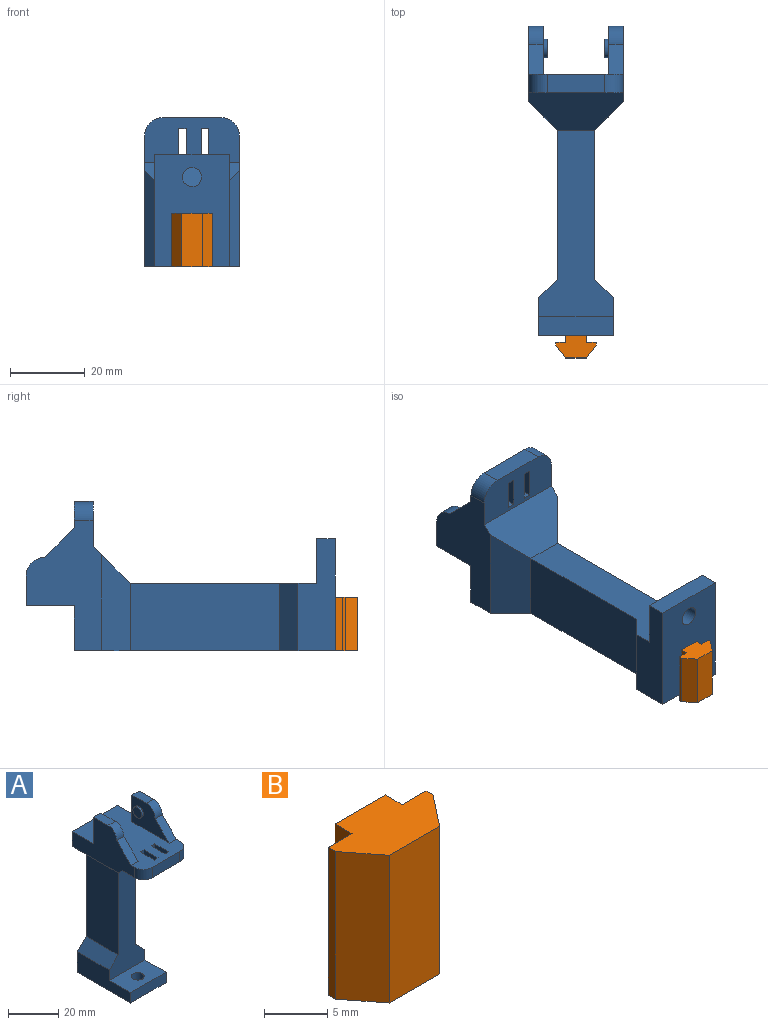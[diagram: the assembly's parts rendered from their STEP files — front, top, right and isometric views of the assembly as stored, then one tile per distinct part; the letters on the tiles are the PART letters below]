
ASSEMBLY  parts=2 mates=1
PART A: 44 faces, bbox 25.5x40x83 mm
  f0: plane 25.5x12mm, normal (0,0,-1), area 263.8mm2, adj f2,f3,f16,f17,f18,f19,f20,f21
  f1: plane 40x25.5mm, normal (0,0,1), area 809.8mm2, adj f2,f3,f5,f6,f8,f9,f16,f17
  f2: plane 15.5x5mm, normal (0,-1,0), area 77.5mm2, adj f0,f1,f25,f27
  f3: plane 35x20.25mm, normal (-1,0,0), area 431.1mm2, adj f0,f1,f5,f7,f14,f24,f25,f39
  f4: plane 8x4mm, normal (0,0,1), area 32mm2, adj f8,f9,f15,f26
  f5: plane 13x4mm, normal (0,1,0), area 52mm2, adj f1,f3,f6,f7
  f6: plane 21x13mm, normal (1,0,0), area 176mm2, adj f1,f5,f7,f12,f14,f41
  f7: plane 8x4mm, normal (0,0,1), area 32mm2, adj f3,f5,f6,f14
  f8: plane 21x13mm, normal (-1,0,0), area 176mm2, adj f1,f4,f9,f10,f15,f40
  f9: plane 13x4mm, normal (0,1,0), area 52mm2, adj f1,f4,f8,f26
  f10: cylinder r=2.5mm len=5mm, axis (1,0,0), area 15.7mm2, adj f8,f11
  f11: plane 5x5mm, normal (-1,0,0), area 19.6mm2, adj f10
  f12: cylinder r=2.5mm len=5mm, axis (-1,0,0), area 15.7mm2, adj f6,f13
  f13: plane 5x5mm, normal (1,0,0), area 19.6mm2, adj f12
  f14: cylinder r=5mm len=5mm, axis (-1,0,0), area 31.4mm2, adj f3,f6,f7,f41
  f15: cylinder r=5mm len=5mm, axis (-1,0,0), area 31.4mm2, adj f4,f8,f26,f40
  f16: plane 7.87x5mm, normal (1,0,0), area 39.4mm2, adj f0,f1,f17,f19
  f17: plane 5x2mm, normal (0,1,0), area 10mm2, adj f0,f1,f16,f18
  f18: plane 7.87x5mm, normal (-1,0,0), area 39.4mm2, adj f0,f1,f17,f19
  f19: plane 5x2mm, normal (0,-1,0), area 10mm2, adj f0,f1,f16,f18
  f20: plane 7.87x5mm, normal (1,0,0), area 39.4mm2, adj f0,f1,f21,f23
  f21: plane 5x2mm, normal (0,1,0), area 10mm2, adj f0,f1,f20,f22
  f22: plane 7.87x5mm, normal (-1,0,0), area 39.4mm2, adj f0,f1,f21,f23
  f23: plane 5x2mm, normal (0,-1,0), area 10mm2, adj f0,f1,f20,f22
  f24: plane 70x25.5mm, normal (0,1,0), area 997.4mm2, adj f1,f3,f26,f28,f30,f32,f33,f34
  f25: cylinder r=5mm len=5mm, axis (0,0,1), area 39.3mm2, adj f0,f1,f2,f3
  f26: plane 35x20.25mm, normal (1,0,0), area 431.1mm2, adj f0,f1,f4,f9,f15,f24,f27,f38
  f27: cylinder r=5mm len=5mm, axis (0,0,1), area 39.3mm2, adj f0,f1,f2,f26
  f28: plane 40x18mm, normal (1,0,0), area 720mm2, adj f24,f29,f36,f38
  f29: plane 50x20mm, normal (0,-1,0), area 575mm2, adj f28,f30,f31,f33,f34,f36,f37,f42
  f30: plane 40x18mm, normal (-1,0,0), area 720mm2, adj f24,f29,f37,f39
  f31: plane 20x12mm, normal (0,0,1), area 219.6mm2, adj f29,f33,f34,f35,f43
  f32: plane 30x20mm, normal (0,0,-1), area 579.6mm2, adj f24,f33,f34,f35,f43
  f33: plane 30x10mm, normal (-1,0,0), area 240mm2, adj f24,f29,f31,f32,f35,f37
  f34: plane 30x10mm, normal (1,0,0), area 240mm2, adj f24,f29,f31,f32,f35,f36
  f35: plane 20x5mm, normal (0,-1,0), area 100mm2, adj f31,f32,f33,f34
  f36: plane 18x5mm, normal (0.71,0,0.71), area 127.3mm2, adj f24,f28,f29,f34
  f37: plane 18x5mm, normal (-0.71,0,0.71), area 127.3mm2, adj f24,f29,f30,f33
  f38: plane 25.75x7.75mm, normal (0.71,0,-0.71), area 239.8mm2, adj f24,f26,f28,f42
  f39: plane 25.75x7.75mm, normal (-0.71,0,-0.71), area 239.8mm2, adj f3,f24,f30,f42
  f40: plane 8x8mm, normal (0,-0.71,0.71), area 45.3mm2, adj f1,f8,f15,f26
  f41: plane 8x8mm, normal (0,-0.71,0.71), area 45.3mm2, adj f1,f3,f6,f14
  f42: plane 25.5x10mm, normal (0,-0.71,-0.71), area 275.7mm2, adj f0,f3,f26,f29,f38,f39
  f43: cylinder r=2.55mm len=5.1mm, axis (0,0,-1), area 80.1mm2, adj f31,f32
PART B: 12 faces, bbox 10.9x6.1x14.3 mm
  f0: plane 14.32x2.65mm, normal (0,1,0), area 38mm2, adj f1,f6,f10,f11
  f1: plane 14.32x0.8mm, normal (-1,0,0), area 11.5mm2, adj f0,f2,f10,f11
  f2: plane 14.32x3.39mm, normal (-0.79,-0.62,0), area 61.7mm2, adj f1,f9,f10,f11
  f3: plane 14.32x3.39mm, normal (0.79,-0.62,0), area 61.7mm2, adj f4,f9,f10,f11
  f4: plane 14.32x0.8mm, normal (1,0,0), area 11.5mm2, adj f3,f5,f10,f11
  f5: plane 14.32x2.65mm, normal (0,1,0), area 38mm2, adj f4,f7,f10,f11
  f6: plane 14.32x1.9mm, normal (-1,0,0), area 27.2mm2, adj f0,f8,f10,f11
  f7: plane 14.32x1.9mm, normal (1,0,0), area 27.2mm2, adj f5,f8,f10,f11
  f8: plane 14.32x5.63mm, normal (0,1,0), area 80.6mm2, adj f6,f7,f10,f11
  f9: plane 14.32x5.63mm, normal (0,-1,0), area 80.6mm2, adj f2,f3,f10,f11
  f10: plane 10.94x6.09mm, normal (0,0,1), area 47.5mm2, adj f0,f1,f2,f3,f4,f5,f6,f7
  f11: plane 10.94x6.09mm, normal (0,0,-1), area 47.5mm2, adj f0,f1,f2,f3,f4,f5,f6,f7
PLACE A rot(axis=(-1,0,0),90deg) t=(-42.36,60.11,-13.2)mm
PLACE B t=(-46.61,19.51,-56.87)mm
MATE fastened A.f32 <-> B.f8  axis (0,-1,0) through (-46.61,-4.89,-38.2)mm
